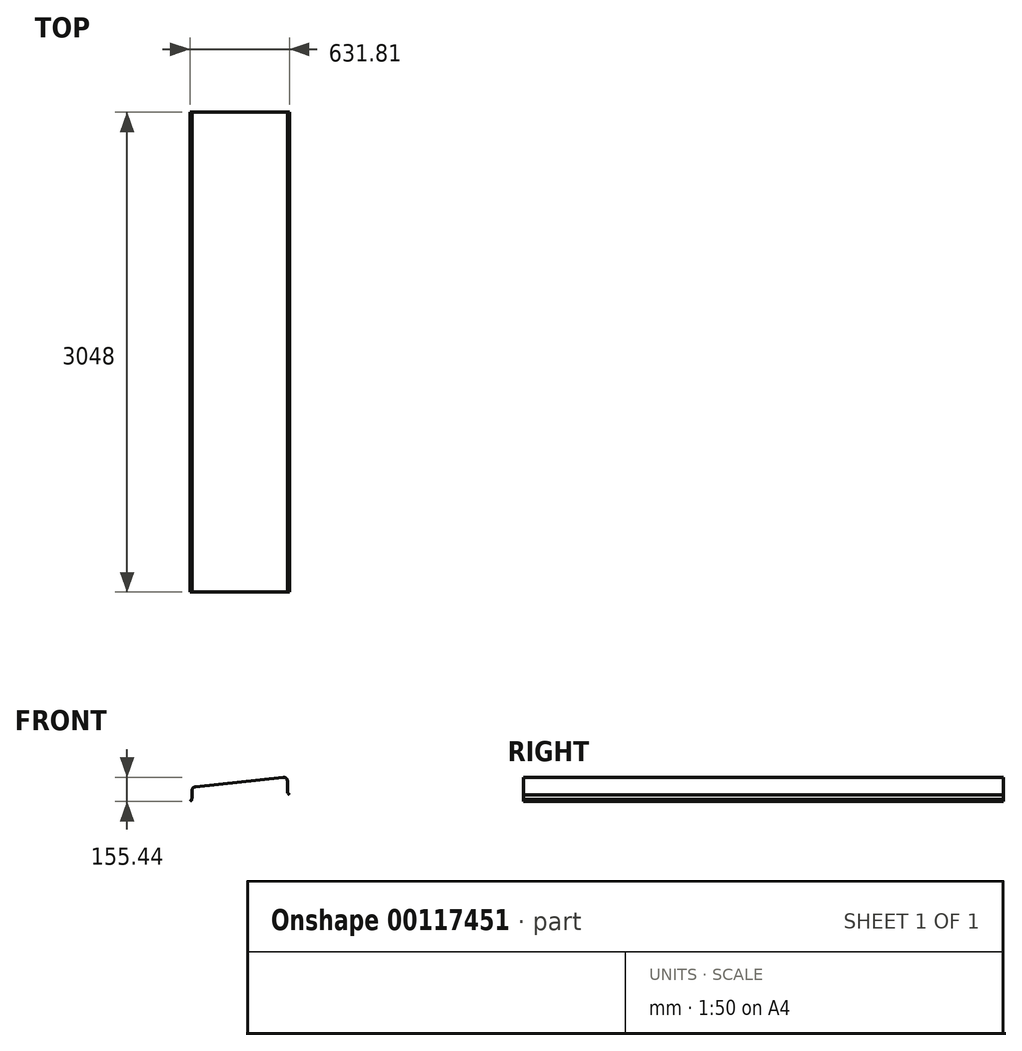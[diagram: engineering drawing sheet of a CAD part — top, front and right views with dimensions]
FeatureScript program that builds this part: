
annotation { "Feature Type Name" : "Feature", "Feature Type Description" : "" }
export const myFeature = defineFeature(function(context is Context, id is Id, definition is map)
    precondition{}
    {
        {
            var Q0;
            Q0=qCreatedBy(makeId("Front.planeOp"),FACE);
            var sketch = newSketch(context, id + "F0", { "sketchPlane" : qUnion([Q0])});
            skLineSegment(sketch, "E0", {"start": v(-319.46, -1.7) * mm, "end": v(-332.24, -15.83) * mm});
            skLineSegment(sketch, "E1", {"start": v(-332.24, -15.83) * mm, "end": v(-334.13, -14.13) * mm});
            skLineSegment(sketch, "E2", {"start": v(-334.13, -14.13) * mm, "end": v(-321.35, 0) * mm});
            skLineSegment(sketch, "E3", {"start": v(-321.35, 0) * mm, "end": v(-321.35, 76.2) * mm});
            skLineSegment(sketch, "E4", {"start": v(-321.35, 76.2) * mm, "end": v(284.63, 142.54) * mm});
            skLineSegment(sketch, "E5", {"start": v(284.63, 142.54) * mm, "end": v(284.63, 40.94) * mm});
            skLineSegment(sketch, "E6", {"start": v(284.63, 40.94) * mm, "end": v(297.68, 27.06) * mm});
            skSolve(sketch);
        }
        {
            var Q0;
            Q0=sQuery(id+"F0.wireOp",EDGE,"E4");
            var Q1;
            Q1=sQuery(id+"F0.wireOp",EDGE,"E3");
            var Q2;
            Q2=sQuery(id+"F0.wireOp",EDGE,"E2");
            var Q3;
            Q3=sQuery(id+"F0.wireOp",EDGE,"E1");
            var Q4;
            Q4=sQuery(id+"F0.wireOp",EDGE,"E0");
            var Q5;
            Q5=sQuery(id+"F0.wireOp",EDGE,"E5");
            var Q6;
            Q6=sQuery(id+"F0.wireOp",EDGE,"E6");
            extrude(context, id + "F1", {"bodyType" : ToolBodyType.SURFACE, "surfaceEntities" : qUnion([Q0, Q1, Q2, Q3, Q4, Q5, Q6]), "depth" : 3048 * mm});
        }
        {
            var Q0;
            Q0=makeQuery(id+"F1.opExtrude","SWEPT_FACE",FACE,{"disambiguationData":[OSD([sQuery(id+"F0.wireOp",EDGE,"E3")])]});
            var Q1;
            Q1=makeQuery(id+"F1.opExtrude","SWEPT_FACE",FACE,{"disambiguationData":[OSD([sQuery(id+"F0.wireOp",EDGE,"E4")])]});
            var Q2;
            Q2=makeQuery(id+"F1.opExtrude","SWEPT_FACE",FACE,{"disambiguationData":[OSD([sQuery(id+"F0.wireOp",EDGE,"E5")])]});
            fillet(context, id + "F2", {"entities" : qUnion([Q0, Q1, Q2]), "radius" : 25.4 * mm, "tangentPropagation" : true, "allowEdgeOverflow" : false});
        }
    });
